# Revit family: FU_Chair_Sandler_Nassau 2-0
name_source: partatom
category: Furniture
units: mm (PartAtom-declared; Revit-internal decimal feet)

## family parameters
Always vertical = Yes
Cut with Voids When Loaded = No
OmniClass Number = 23.40.20.00
OmniClass Title = General Furniture and Specialties
Room Calculation Point = No
Shared = No
Work Plane-Based = No

## types (1)
- Nassau 2.0
    Default Elevation = 0 mm  [stored 0 ft]
    Depth = 490 mm  [stored 1.60761 ft]
    Description = Air molded polypropylene monobloc armchair, stacks 8 high. Can only be ordered in multiples of 4, per color. MOQ 4 pcs.
    Height = 820 mm  [stored 2.69029 ft]
    Manufacturer = Sandler
    Model = Nassau 2.0
    Polypropylene = Polypropylene - Anthracite Grey - NCS S7502-B
    URL = https://www.sandlerseating.com
    Width = 530 mm  [stored 1.73885 ft]

note: [stored X ft] marks values corroborated as IEEE doubles in the binary element streams (Revit-internal decimal feet)

## geometry (parser evidence)
native form markers: Sweep x3
no freeform markers — native parametric forms only
